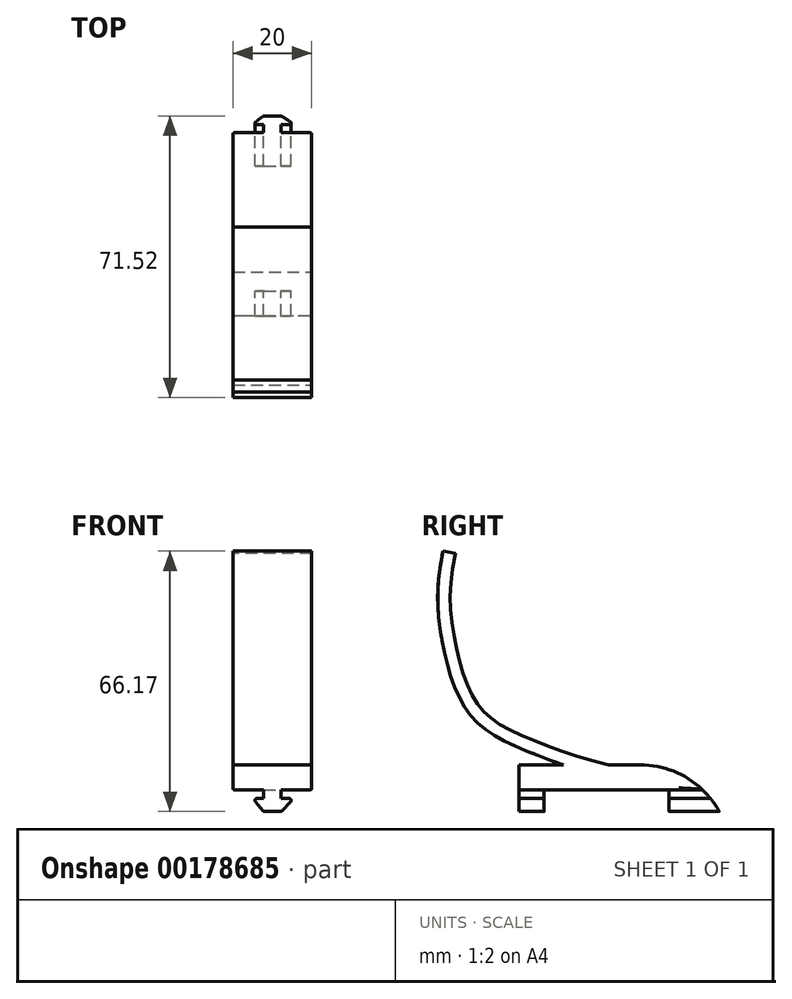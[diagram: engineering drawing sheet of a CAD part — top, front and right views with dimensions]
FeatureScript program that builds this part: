
annotation { "Feature Type Name" : "Feature", "Feature Type Description" : "" }
export const myFeature = defineFeature(function(context is Context, id is Id, definition is map)
    precondition{}
    {
        {
            var Q0;
            Q0=qCreatedBy(makeId("Front.planeOp"),FACE);
            var sketch = newSketch(context, id + "F0", { "sketchPlane" : qUnion([Q0])});
            skLineSegment(sketch, "E0", {"start": v(0, -2.25) * mm, "end": v(0, 2.25) * mm});
            skLineSegment(sketch, "E1", {"start": v(0, 2.25) * mm, "end": v(-2.2, 2.25) * mm});
            skLineSegment(sketch, "E2", {"start": v(-2.2, 2.25) * mm, "end": v(-2.2, 3.92) * mm});
            skLineSegment(sketch, "E3", {"start": v(-3.03, 4.3) * mm, "end": v(-5.32, 2.4) * mm});
            skLineSegment(sketch, "E4", {"start": v(-5.5, 2.01) * mm, "end": v(-5.5, -2.04) * mm});
            skLineSegment(sketch, "E5", {"start": v(-5.35, -2.4) * mm, "end": v(-3.06, -4.64) * mm});
            skLineSegment(sketch, "E6", {"start": v(-2.2, -4.28) * mm, "end": v(-2.2, -2.25) * mm});
            skLineSegment(sketch, "E7", {"start": v(-2.2, -2.25) * mm, "end": v(0, -2.25) * mm});
            skPoint(sketch, "E8", {"position": v(-5.5, 0) * mm});
            skLineSegment(sketch, "E9.bottom", {"start": v(0.5, -10) * mm, "end": v(6.35, -10) * mm});
            skLineSegment(sketch, "E9.top", {"start": v(0.5, 10) * mm, "end": v(6.35, 10) * mm});
            skLineSegment(sketch, "E9.left", {"start": v(0, -9.5) * mm, "end": v(0, 9.5) * mm});
            skLineSegment(sketch, "E9.right", {"start": v(6.35, -10) * mm, "end": v(6.35, 10) * mm});
            skPoint(sketch, "E10", {"position": v(6.35, 0) * mm});
            skPoint(sketch, "E11.visualSharp", {"position": v(-2.2, 5) * mm});
            skArc(sketch, "E11.filletArc", {"start": v(-2.2, 3.92) * mm, "mid": v(-2.5, 4.38) * mm, "end": v(-3.03, 4.3) * mm});
            skPoint(sketch, "E12.visualSharp", {"position": v(0, -10) * mm});
            skArc(sketch, "E12.filletArc", {"start": v(0, -9.5) * mm, "mid": v(0.15, -9.85) * mm, "end": v(0.5, -10) * mm});
            skPoint(sketch, "E13.visualSharp", {"position": v(-2.2, -5.5) * mm});
            skArc(sketch, "E13.filletArc", {"start": v(-3.06, -4.64) * mm, "mid": v(-2.51, -4.75) * mm, "end": v(-2.2, -4.28) * mm});
            skPoint(sketch, "E14.visualSharp", {"position": v(-5.5, -2.25) * mm});
            skArc(sketch, "E14.filletArc", {"start": v(-5.5, -2.04) * mm, "mid": v(-5.46, -2.23) * mm, "end": v(-5.35, -2.4) * mm});
            skPoint(sketch, "E15.visualSharp", {"position": v(-5.5, 2.25) * mm});
            skArc(sketch, "E15.filletArc", {"start": v(-5.32, 2.4) * mm, "mid": v(-5.45, 2.23) * mm, "end": v(-5.5, 2.01) * mm});
            skPoint(sketch, "E16.visualSharp", {"position": v(0, 10) * mm});
            skArc(sketch, "E16.filletArc", {"start": v(0.5, 10) * mm, "mid": v(0.15, 9.85) * mm, "end": v(0, 9.5) * mm});
            skSolve(sketch);
        }
        {
            var Q0;
            Q0=qSketchRegion(id+"F0",true);
            extrude(context, id + "F1", {"entities" : qUnion([Q0]), "depth" : 50.8 * mm});
        }
        {
            var Q0;
            Q0=makeQuery(id+"F1.opExtrude","SWEPT_BODY",BODY,{"disambiguationData":[OSD([sQuery(id+"F0.wireOp",EDGE,"E1"),sQuery(id+"F0.wireOp",EDGE,"E2"),sQuery(id+"F0.wireOp",EDGE,"E3"),sQuery(id+"F0.wireOp",EDGE,"E4"),sQuery(id+"F0.wireOp",EDGE,"E5"),sQuery(id+"F0.wireOp",EDGE,"E6"),sQuery(id+"F0.wireOp",EDGE,"E7"),sQuery(id+"F0.wireOp",EDGE,"E9.bottom"),sQuery(id+"F0.wireOp",EDGE,"E9.top"),sQuery(id+"F0.wireOp",EDGE,"E9.left"),sQuery(id+"F0.wireOp",EDGE,"E9.right"),sQuery(id+"F0.wireOp",EDGE,"E11.filletArc"),sQuery(id+"F0.wireOp",EDGE,"E12.filletArc"),sQuery(id+"F0.wireOp",EDGE,"E13.filletArc"),sQuery(id+"F0.wireOp",EDGE,"E14.filletArc"),sQuery(id+"F0.wireOp",EDGE,"E15.filletArc"),sQuery(id+"F0.wireOp",EDGE,"E16.filletArc")])]});
            var Q1;
            Q1=makeQuery(id+"F1.opExtrude","SWEPT_EDGE",EDGE,{"disambiguationData":[OSD([sQuery(id+"F0.wireOp",EDGE,"E9.top"),sQuery(id+"F0.wireOp",EDGE,"E9.right")])]});
            var Q2;
            Q2=makeQuery(id+"F1.opExtrude","SWEPT_EDGE",EDGE,{"disambiguationData":[OSD([sQuery(id+"F0.wireOp",EDGE,"E9.top"),sQuery(id+"F0.wireOp",EDGE,"E9.right")])]});
            transform(context, id + "F2", {"entities" : qUnion([Q0]), "transformType" : TransformType.ROTATION, "transformAxis" : qUnion([Q2]), "angle" : 270 * degree, "makeCopy" : false});
        }
        {
            var Q0;
            Q0=qCreatedBy(makeId("Right.planeOp"),FACE);
            cPlane(context, id + "F3", {"entities" : qUnion([Q0]), "cplaneType" : CPlaneType.OFFSET, "offset" : 16.5 * mm, "width" : 152.4 * mm, "height" : 152.4 * mm});
        }
        {
            var Q0;
            Q0=qCreatedBy(id+"F3.planeOp",FACE);
            var sketch = newSketch(context, id + "F4", { "sketchPlane" : qUnion([Q0])});
            skFitSpline(sketch, "E17", {"points": [v(0, 1.28) * mm, v(-47, 10.2) * mm, v(-64.5, 20.44) * mm, v(-72.46, 39.71) * mm, v(-72.46, 64.78) * mm], "startDerivative": vector(-220.03, 5.13) * mm, "endDerivative": vector(27.6, 122.78) * mm});
            skSolve(sketch);
        }
        {
            var Q0;
            Q0=makeQuery(id+"F1.opExtrude","CAP_FACE",FACE,{"disambiguationData":[OSD([sQuery(id+"F0.wireOp",EDGE,"E1"),sQuery(id+"F0.wireOp",EDGE,"E2"),sQuery(id+"F0.wireOp",EDGE,"E3"),sQuery(id+"F0.wireOp",EDGE,"E4"),sQuery(id+"F0.wireOp",EDGE,"E5"),sQuery(id+"F0.wireOp",EDGE,"E6"),sQuery(id+"F0.wireOp",EDGE,"E7"),sQuery(id+"F0.wireOp",EDGE,"E9.bottom"),sQuery(id+"F0.wireOp",EDGE,"E9.top"),sQuery(id+"F0.wireOp",EDGE,"E9.left"),sQuery(id+"F0.wireOp",EDGE,"E9.right"),sQuery(id+"F0.wireOp",EDGE,"E11.filletArc"),sQuery(id+"F0.wireOp",EDGE,"E12.filletArc"),sQuery(id+"F0.wireOp",EDGE,"E13.filletArc"),sQuery(id+"F0.wireOp",EDGE,"E14.filletArc"),sQuery(id+"F0.wireOp",EDGE,"E15.filletArc"),sQuery(id+"F0.wireOp",EDGE,"E16.filletArc")])],"isStart":true});
            var sketch = newSketch(context, id + "F5", { "sketchPlane" : qUnion([Q0])});
            skLineSegment(sketch, "E18.bottom", {"start": v(-26.35, 3.65) * mm, "end": v(-6.35, 3.65) * mm});
            skLineSegment(sketch, "E18.top", {"start": v(-26.35, 6.82) * mm, "end": v(-6.35, 6.82) * mm});
            skLineSegment(sketch, "E18.left", {"start": v(-26.35, 3.65) * mm, "end": v(-26.35, 6.82) * mm});
            skLineSegment(sketch, "E18.right", {"start": v(-6.35, 3.65) * mm, "end": v(-6.35, 6.82) * mm});
            skSolve(sketch);
        }
        {
            var Q0;
            Q0 = qSketchRegion(id + "F5", true);
            var Q1;
            Q1 = qConstructionFilter(qBodyType(qCreatedBy(id + "F4" ,EDGE), BodyType.WIRE), ConstructionObject.NO);
            sweep(context, id + "F6", {"operationType" : NewBodyOperationType.ADD, "profiles" : qUnion([Q0]), "path" : qUnion([Q1])});
        }
        {
            var Q0;
            Q0=makeQuery(id+"F6.boolean.opBoolean","MERGE",FACE,{"derivedFrom":[makeQuery(id+"F1.opExtrude","CAP_FACE",FACE,{"disambiguationData":[OSD([sQuery(id+"F0.wireOp",EDGE,"E1"),sQuery(id+"F0.wireOp",EDGE,"E2"),sQuery(id+"F0.wireOp",EDGE,"E3"),sQuery(id+"F0.wireOp",EDGE,"E4"),sQuery(id+"F0.wireOp",EDGE,"E5"),sQuery(id+"F0.wireOp",EDGE,"E6"),sQuery(id+"F0.wireOp",EDGE,"E7"),sQuery(id+"F0.wireOp",EDGE,"E9.bottom"),sQuery(id+"F0.wireOp",EDGE,"E9.top"),sQuery(id+"F0.wireOp",EDGE,"E9.left"),sQuery(id+"F0.wireOp",EDGE,"E9.right"),sQuery(id+"F0.wireOp",EDGE,"E11.filletArc"),sQuery(id+"F0.wireOp",EDGE,"E12.filletArc"),sQuery(id+"F0.wireOp",EDGE,"E13.filletArc"),sQuery(id+"F0.wireOp",EDGE,"E14.filletArc"),sQuery(id+"F0.wireOp",EDGE,"E15.filletArc"),sQuery(id+"F0.wireOp",EDGE,"E16.filletArc")])],"isStart":true}),makeQuery(id+"F6.opSweep","CAP_FACE",FACE,{"disambiguationData":[OSD([sQuery(id+"F4.wireOp",VERTEX,"E17.start"),sQuery(id+"F5.wireOp",EDGE,"E18.bottom"),sQuery(id+"F5.wireOp",EDGE,"E18.top"),sQuery(id+"F5.wireOp",EDGE,"E18.left"),sQuery(id+"F5.wireOp",EDGE,"E18.right")])],"isStart":true})]});
            cPlane(context, id + "F7", {"entities" : qUnion([Q0]), "cplaneType" : CPlaneType.OFFSET, "offset" : 12.7 * mm, "oppositeDirection" : true, "width" : 152.4 * mm, "height" : 152.4 * mm});
        }
        {
            var Q0;
            Q0=qCreatedBy(id+"F7.planeOp",FACE);
            var sketch = newSketch(context, id + "F8", { "sketchPlane" : qUnion([Q0])});
            skLineSegment(sketch, "E19.bottom", {"start": v(-10.65, 3.65) * mm, "end": v(-22.08, 3.65) * mm});
            skLineSegment(sketch, "E19.top", {"start": v(-10.65, -1.85) * mm, "end": v(-22.08, -1.85) * mm});
            skLineSegment(sketch, "E19.left", {"start": v(-10.65, 3.65) * mm, "end": v(-10.65, -1.85) * mm});
            skLineSegment(sketch, "E19.right", {"start": v(-22.08, 3.65) * mm, "end": v(-22.08, -1.85) * mm});
            skPoint(sketch, "E20", {"position": v(-16.36, -1.85) * mm});
            skSolve(sketch);
        }
        {
            var Q0;
            Q0 = qSketchRegion(id + "F8", true);
            extrude(context, id + "F9", {"entities" : qUnion([Q0]), "operationType" : NewBodyOperationType.REMOVE, "oppositeDirection" : true, "depth" : 31.75 * mm});
        }
        {
            var Q0;
            Q0=makeQuery(id+"F1.opExtrude","CAP_EDGE",EDGE,{"disambiguationData":[OSD([sQuery(id+"F0.wireOp",EDGE,"E9.right")])],"isStart":true});
            fillet(context, id + "F10", {"entities" : qUnion([Q0]), "radius" : 22.86 * mm, "allowEdgeOverflow" : false});
        }
        {
            var Q0;
            Q0=makeQuery(id+"F9.boolean.opBoolean","COPY",EDGE,{"derivedFrom":makeQuery(id+"F9.opExtrude","CAP_EDGE",EDGE,{"disambiguationData":[OSD([sQuery(id+"F8.wireOp",EDGE,"E19.bottom")])],"isStart":false})});
            cPlane(context, id + "F11", {"entities" : qUnion([Q0]), "cplaneType" : CPlaneType.LINE_ANGLE, "offset" : 25.4 * mm, "angle" : 80 * degree, "width" : 152.4 * mm, "height" : 152.4 * mm});
        }
    });
